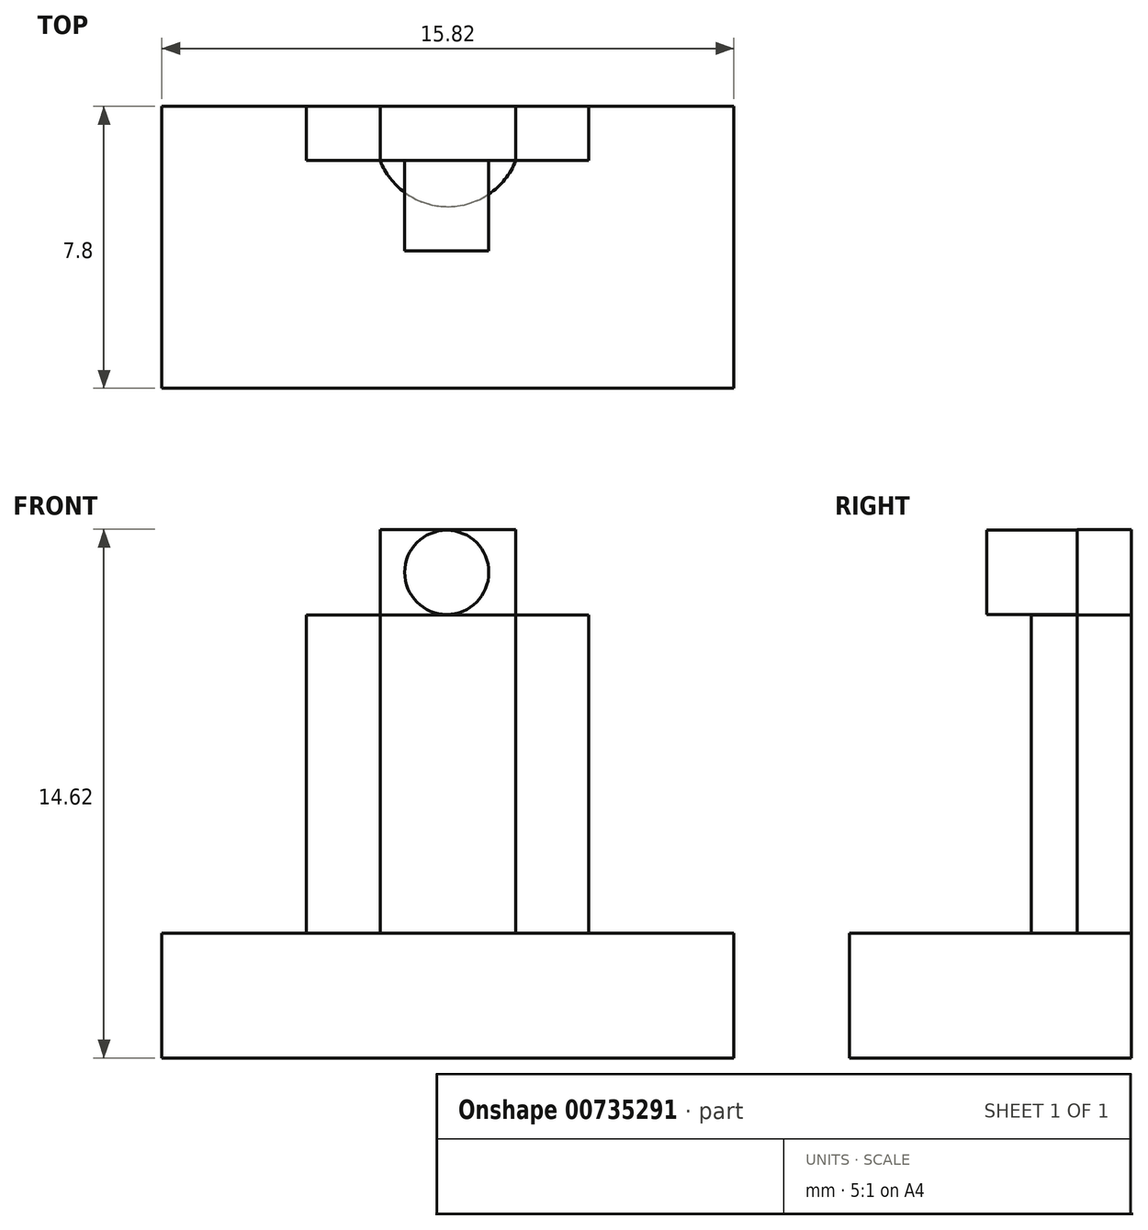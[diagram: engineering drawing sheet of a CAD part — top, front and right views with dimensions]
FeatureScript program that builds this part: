
annotation { "Feature Type Name" : "Feature", "Feature Type Description" : "" }
export const myFeature = defineFeature(function(context is Context, id is Id, definition is map)
    precondition{}
    {
        {
            var Q0;
            Q0=qCreatedBy(makeId("Front.planeOp"),FACE);
            var sketch = newSketch(context, id + "F0", { "sketchPlane" : qUnion([Q0])});
            skLineSegment(sketch, "E0", {"start": v(0, 0) * mm, "end": v(0, 3.45) * mm});
            skLineSegment(sketch, "E1", {"start": v(0, 3.45) * mm, "end": v(15.82, 3.45) * mm});
            skLineSegment(sketch, "E2", {"start": v(15.82, 3.45) * mm, "end": v(15.82, 0) * mm});
            skLineSegment(sketch, "E3", {"start": v(15.82, 0) * mm, "end": v(0, 0) * mm});
            skSolve(sketch);
        }
        {
            var Q0;
            Q0 = qSketchRegion(id + "F0", true);
            extrude(context, id + "F1", {"entities" : qUnion([Q0]), "depth" : 7.8 * mm, "offsetDistance" : 25 * mm});
        }
        {
            var Q0;
            Q0=makeQuery(id+"F1.opExtrude","SWEPT_FACE",FACE,{"disambiguationData":[OSD([sQuery(id+"F0.wireOp",EDGE,"E1")])]});
            var sketch = newSketch(context, id + "F2", { "sketchPlane" : qUnion([Q0])});
            skLineSegment(sketch, "E4", {"start": v(11.81, 0) * mm, "end": v(11.81, -1.5) * mm});
            skLineSegment(sketch, "E5", {"start": v(11.81, -1.5) * mm, "end": v(4, -1.5) * mm});
            skLineSegment(sketch, "E6", {"start": v(4, -1.5) * mm, "end": v(4, 0) * mm});
            skLineSegment(sketch, "E7", {"start": v(11.81, 0) * mm, "end": v(4, 0) * mm});
            skLineSegment(sketch, "E8", {"start": v(4, -1.5) * mm, "end": v(6.04, -1.5) * mm});
            skLineSegment(sketch, "E9", {"start": v(11.81, -1.5) * mm, "end": v(9.8, -1.5) * mm});
            skArc(sketch, "E10", {"start": v(6.04, -1.5) * mm, "mid": v(7.91, -2.77) * mm, "end": v(9.8, -1.5) * mm});
            skSolve(sketch);
        }
        {
            var Q0;
            Q0 = qSketchRegion(id + "F2", true);
            extrude(context, id + "F3", {"entities" : qUnion([Q0]), "operationType" : NewBodyOperationType.ADD, "depth" : 8.8 * mm, "offsetDistance" : 25 * mm});
        }
        {
            var Q0;
            Q0=makeQuery(id+"F3.opExtrude","CAP_FACE",FACE,{"disambiguationData":[OSD([sQuery(id+"F2.wireOp",EDGE,"E4"),sQuery(id+"F2.wireOp",EDGE,"E6"),sQuery(id+"F2.wireOp",EDGE,"E7"),sQuery(id+"F2.wireOp",EDGE,"E8"),sQuery(id+"F2.wireOp",EDGE,"E9"),sQuery(id+"F2.wireOp",EDGE,"E10")])],"isStart":false});
            var sketch = newSketch(context, id + "F4", { "sketchPlane" : qUnion([Q0])});
            skLineSegment(sketch, "E11", {"start": v(6.04, -1.5) * mm, "end": v(6.04, 0) * mm});
            skLineSegment(sketch, "E12", {"start": v(6.04, 0) * mm, "end": v(9.8, 0) * mm});
            skLineSegment(sketch, "E13", {"start": v(9.8, 0) * mm, "end": v(9.8, -1.5) * mm});
            skLineSegment(sketch, "E14", {"start": v(9.8, -1.5) * mm, "end": v(6.04, -1.5) * mm});
            skSolve(sketch);
        }
        {
            var Q0;
            Q0 = qSketchRegion(id + "F4", true);
            extrude(context, id + "F5", {"entities" : qUnion([Q0]), "operationType" : NewBodyOperationType.ADD, "depth" : 2.37 * mm, "offsetDistance" : 25 * mm});
        }
        {
            var Q0;
            Q0=makeQuery(id+"F5.opExtrude","SWEPT_FACE",FACE,{"disambiguationData":[OSD([sQuery(id+"F4.wireOp",EDGE,"E14")])]});
            var sketch = newSketch(context, id + "F6", { "sketchPlane" : qUnion([Q0])});
            skCircle(sketch, "E15", {"center": v(7.88, 13.43) * mm, "radius": 1.16 * mm});
            skSolve(sketch);
        }
        {
            var Q0;
            Q0 = qSketchRegion(id + "F6", true);
            extrude(context, id + "F7", {"entities" : qUnion([Q0]), "operationType" : NewBodyOperationType.ADD, "depth" : 2.5 * mm, "offsetDistance" : 25 * mm});
        }
    });
